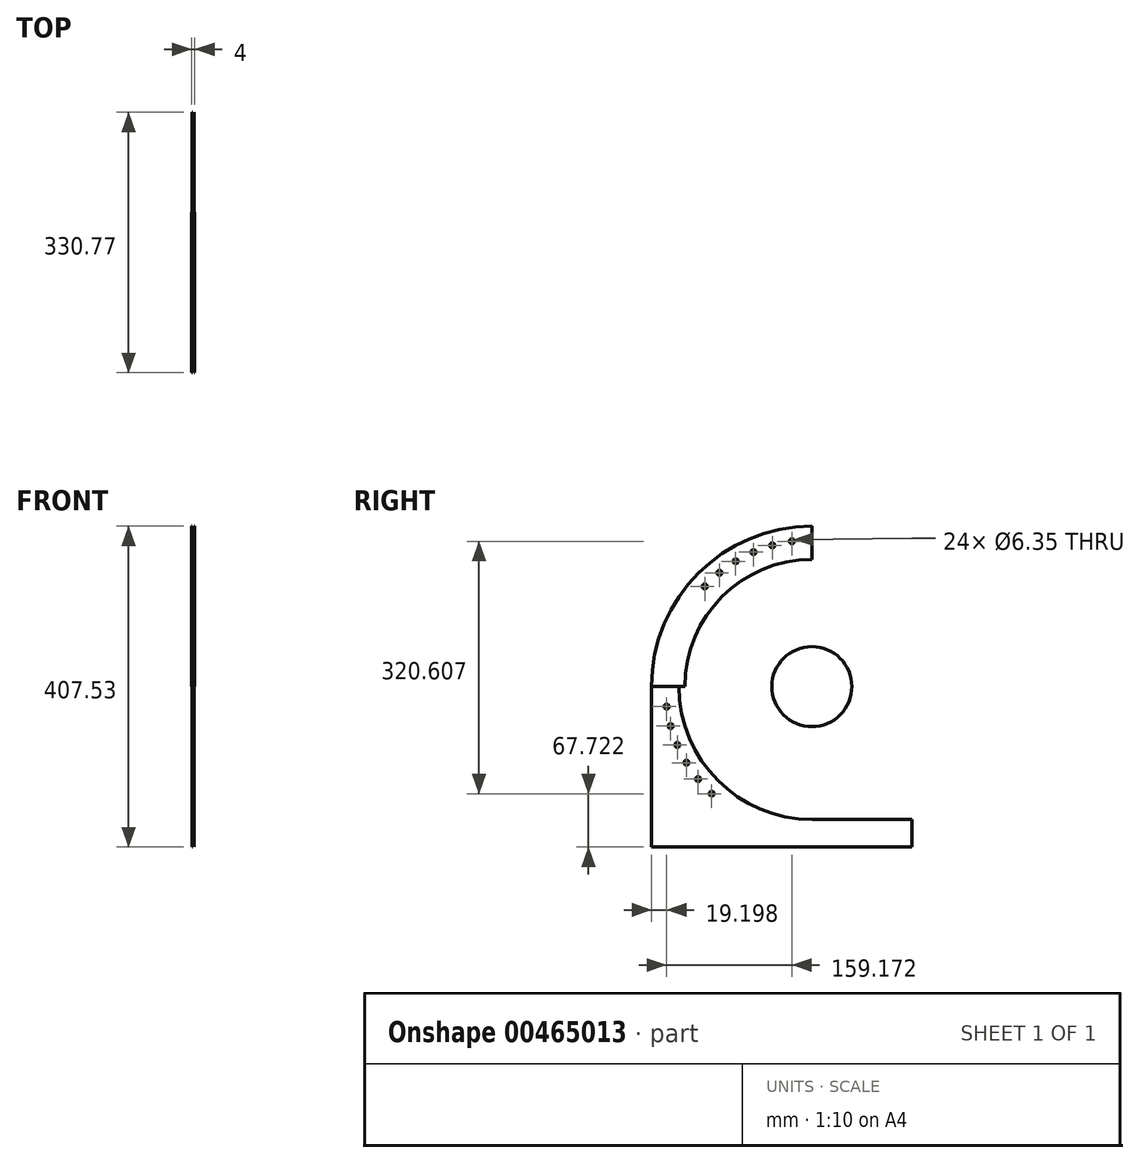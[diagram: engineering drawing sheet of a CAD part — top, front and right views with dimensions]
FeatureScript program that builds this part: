
annotation { "Feature Type Name" : "Feature", "Feature Type Description" : "" }
export const myFeature = defineFeature(function(context is Context, id is Id, definition is map)
    precondition{}
    {
        {
            assignVariable(context, id + "F0", {"name" : "trw", "anyValue" : .5});
        }
        {
            assignVariable(context, id + "F1", {"name" : "trsp", "anyValue" : 2});
        }
        {
            assignVariable(context, id + "F2", {"name" : "shwhw", "anyValue" : 2});
        }
        {
            var Q0;
            Q0=qCreatedBy(makeId("Right.planeOp"),FACE);
            cPlane(context, id + "F3", {"entities" : qUnion([Q0]), "cplaneType" : CPlaneType.OFFSET, "offset" : (getVariable(context, 'trsp') / 2) * mm, "width" : 152.4 * mm, "height" : 152.4 * mm});
        }
        {
            var Q0;
            Q0=qCreatedBy(id+"F3.planeOp",FACE);
            var sketch = newSketch(context, id + "F4", { "sketchPlane" : qUnion([Q0])});
            skLineSegment(sketch, "E0.bottom", {"start": v(0, 0) * mm, "end": v(127, 0) * mm});
            skLineSegment(sketch, "E0.top", {"start": v(0, 34.93) * mm, "end": v(127, 34.93) * mm});
            skLineSegment(sketch, "E0.left", {"start": v(0, 0) * mm, "end": v(0, 34.93) * mm});
            skLineSegment(sketch, "E0.right", {"start": v(127, 0) * mm, "end": v(127, 34.92) * mm});
            skCircle(sketch, "E1", {"center": v(0, 203.77) * mm, "radius": 50.8 * mm});
            skArc(sketch, "E2", {"start": v(-168.84, 203.77) * mm, "mid": v(-119.39, 84.38) * mm, "end": v(0, 34.93) * mm});
            skArc(sketch, "E3", {"start": v(-203.77, 203.77) * mm, "mid": v(-144.08, 59.68) * mm, "end": v(0, 0) * mm});
            skLineSegment(sketch, "E4", {"start": v(-168.84, 203.77) * mm, "end": v(-203.77, 203.77) * mm});
            skLineSegment(sketch, "E5", {"start": v(0, 0) * mm, "end": v(-203.77, 0) * mm});
            skLineSegment(sketch, "E6", {"start": v(-203.77, 0) * mm, "end": v(-203.77, 203.77) * mm});
            skPoint(sketch, "E7", {"position": v(-186.3, 203.77) * mm});
            skCircle(sketch, "E8", {"center": v(0, 203.77) * mm, "radius": 186.3 * mm, "construction": true});
            skCircle(sketch, "E9", {"center": v(-184.57, 178.42) * mm, "radius": 3.18 * mm});
            skCircle(sketch, "E10.1.0", {"center": v(-179.4, 153.55) * mm, "radius": 3.18 * mm});
            skCircle(sketch, "E10.2.0", {"center": v(-170.91, 129.62) * mm, "radius": 3.18 * mm});
            skCircle(sketch, "E10.3.0", {"center": v(-159.24, 107.06) * mm, "radius": 3.17 * mm});
            skCircle(sketch, "E10.4.0", {"center": v(-144.6, 86.3) * mm, "radius": 3.18 * mm});
            skCircle(sketch, "E10.5.0", {"center": v(-127.28, 67.72) * mm, "radius": 3.18 * mm});
            skLineSegment(sketch, "E10.anchor1", {"start": v(0, 203.77) * mm, "end": v(-184.57, 178.42) * mm, "construction": true});
            skLineSegment(sketch, "E10.anchor2", {"start": v(0, 203.77) * mm, "end": v(-127.28, 67.72) * mm, "construction": true});
            skCircle(sketch, "E11", {"center": v(-0.4, 89.47) * mm, "radius": 63.5 * mm, "construction": true});
            skSolve(sketch);
        }
        {
            var Q0;
            Q0=makeQuery(id+"F4.imprint","IMPRINT",FACE,{"disambiguationData":[TD([[makeQuery(id+"F4.imprint","IMPRINT",EDGE,{"derivedFrom":sQuery(id+"F4.wireOp",EDGE,"E1")}),1.0]])]});
            extrude(context, id + "F5", {"entities" : qUnion([Q0]), "depth" : (getVariable(context, 'shwhw')) * mm});
        }
        {
            var Q0;
            Q0=makeQuery(id+"F4.imprint","IMPRINT",FACE,{"disambiguationData":[TD([[makeQuery(id+"F4.imprint","IMPRINT",EDGE,{"derivedFrom":sQuery(id+"F4.wireOp",EDGE,"E0.left")}),1.0]])]});
            var Q1;
            Q1=makeQuery(id+"F4.imprint","IMPRINT",FACE,{"disambiguationData":[TD([[makeQuery(id+"F4.imprint","IMPRINT",EDGE,{"derivedFrom":sQuery(id+"F4.wireOp",EDGE,"E0.bottom")}),1.0]])]});
            extrude(context, id + "F6", {"entities" : qUnion([Q0, Q1]), "depth" : (getVariable(context, 'trw')) * mm});
        }
        {
            var Q0;
            Q0=makeQuery(id+"F4.imprint","IMPRINT",FACE,{"disambiguationData":[TD([[makeQuery(id+"F4.imprint","IMPRINT",EDGE,{"derivedFrom":sQuery(id+"F4.wireOp",EDGE,"E3")}),-1.0]])]});
            extrude(context, id + "F7", {"entities" : qUnion([Q0]), "operationType" : NewBodyOperationType.ADD, "depth" : (getVariable(context, 'trw')) * mm});
        }
        {
            var Q0;
            Q0=qCreatedBy(makeId("Right.planeOp"),FACE);
            cPlane(context, id + "F8", {"entities" : qUnion([Q0]), "cplaneType" : CPlaneType.OFFSET, "offset" : (getVariable(context, 'trsp') / 2 + getVariable(context, 'trw')) * mm, "width" : 152.4 * mm, "height" : 152.4 * mm});
        }
        {
            var Q0;
            Q0=qCreatedBy(id+"F8.planeOp",FACE);
            var sketch = newSketch(context, id + "F9", { "sketchPlane" : qUnion([Q0])});
            skCircle(sketch, "E12.0.0", {"center": v(0, 203.77) * mm, "radius": 50.8 * mm});
            skArc(sketch, "E13", {"start": v(0, 365.21) * mm, "mid": v(-114.16, 317.93) * mm, "end": v(-161.45, 203.77) * mm});
            skArc(sketch, "E14", {"start": v(0, 407.53) * mm, "mid": v(-144.08, 347.85) * mm, "end": v(-203.77, 203.77) * mm});
            skLineSegment(sketch, "E15", {"start": v(0, 407.53) * mm, "end": v(0, 365.21) * mm});
            skCircle(sketch, "E16", {"center": v(-25.4, 388.33) * mm, "radius": 3.18 * mm});
            skCircle(sketch, "E17.1.0", {"center": v(-50.27, 383.16) * mm, "radius": 3.18 * mm});
            skCircle(sketch, "E17.2.0", {"center": v(-74.2, 374.65) * mm, "radius": 3.18 * mm});
            skCircle(sketch, "E17.3.0", {"center": v(-96.76, 362.97) * mm, "radius": 3.17 * mm});
            skCircle(sketch, "E17.4.0", {"center": v(-117.51, 348.33) * mm, "radius": 3.18 * mm});
            skCircle(sketch, "E17.5.0", {"center": v(-136.08, 331) * mm, "radius": 3.18 * mm});
            skLineSegment(sketch, "E17.anchor1", {"start": v(0, 203.77) * mm, "end": v(-25.4, 388.33) * mm, "construction": true});
            skLineSegment(sketch, "E17.anchor2", {"start": v(0, 203.77) * mm, "end": v(-136.08, 331) * mm, "construction": true});
            skLineSegment(sketch, "E18", {"start": v(-203.77, 203.77) * mm, "end": v(-161.45, 203.77) * mm});
            skCircle(sketch, "E19", {"center": v(2.74, 322.24) * mm, "radius": 63.5 * mm, "construction": true});
            skSolve(sketch);
        }
        {
            var Q0;
            {var subQ0=sQuery(id+"F9.wireOp",EDGE,"E13");Q0=makeQuery(id+"F9.imprint","IMPRINT",FACE,{"disambiguationData":[TD([[makeQuery(id+"F9.imprint","IMPRINT",EDGE,{"derivedFrom":subQ0}),-1.0]])]});}
            extrude(context, id + "F10", {"entities" : qUnion([Q0]), "depth" : (getVariable(context, 'trw')) * mm});
        }
        {
            var Q0;
            Q0=makeQuery(id+"F10.opExtrude","SWEPT_BODY",BODY,{"disambiguationData":[OSD([sQuery(id+"F9.wireOp",EDGE,"E13"),sQuery(id+"F9.wireOp",EDGE,"E14"),sQuery(id+"F9.wireOp",EDGE,"E15"),sQuery(id+"F9.wireOp",EDGE,"f6HUIWgw-bvyF-JxAT-r7YP-LFZp2MHQltQE")])]});
            var Q1;
            Q1=makeQuery(id+"F5.opExtrude","SWEPT_BODY",BODY,{"disambiguationData":[OSD([sQuery(id+"F4.wireOp",EDGE,"E1")])]});
            var Q2;
            Q2=makeQuery(id+"F6.opExtrude","SWEPT_BODY",BODY,{"disambiguationData":[OSD([sQuery(id+"F4.wireOp",EDGE,"E0.bottom"),sQuery(id+"F4.wireOp",EDGE,"E0.top"),sQuery(id+"F4.wireOp",EDGE,"E0.right"),sQuery(id+"F4.wireOp",EDGE,"E2"),sQuery(id+"F4.wireOp",EDGE,"E3"),sQuery(id+"F4.wireOp",EDGE,"E4")])]});
            var Q3;
            Q3=qCreatedBy(makeId("Right.planeOp"),FACE);
            mirror(context, id + "F11", {"entities" : qUnion([Q0, Q1, Q2]), "mirrorPlane" : qUnion([Q3])});
        }
        {
            var Q0;
            Q0=makeQuery(id+"F11.opPattern","COPY",BODY,{"derivedFrom":makeQuery(id+"F5.opExtrude","SWEPT_BODY",BODY,{"disambiguationData":[OSD([sQuery(id+"F4.wireOp",EDGE,"E1")])]}),"instanceName":"1"});
            deleteBodies(context, id + "F12", {"entities" : qUnion([Q0])});
        }
        {
            var Q0;
            Q0=makeQuery(id+"F5.opExtrude","SWEPT_BODY",BODY,{"disambiguationData":[OSD([sQuery(id+"F4.wireOp",EDGE,"E1")])]});
            transform(context, id + "F13", {"entities" : qUnion([Q0]), "transformType" : TransformType.TRANSLATION_3D, "dx" : (-(getVariable(context, 'shwhw'))) * mm, "dy" : 0 * mm, "dz" : 0 * mm, "makeCopy" : false});
        }
    });
